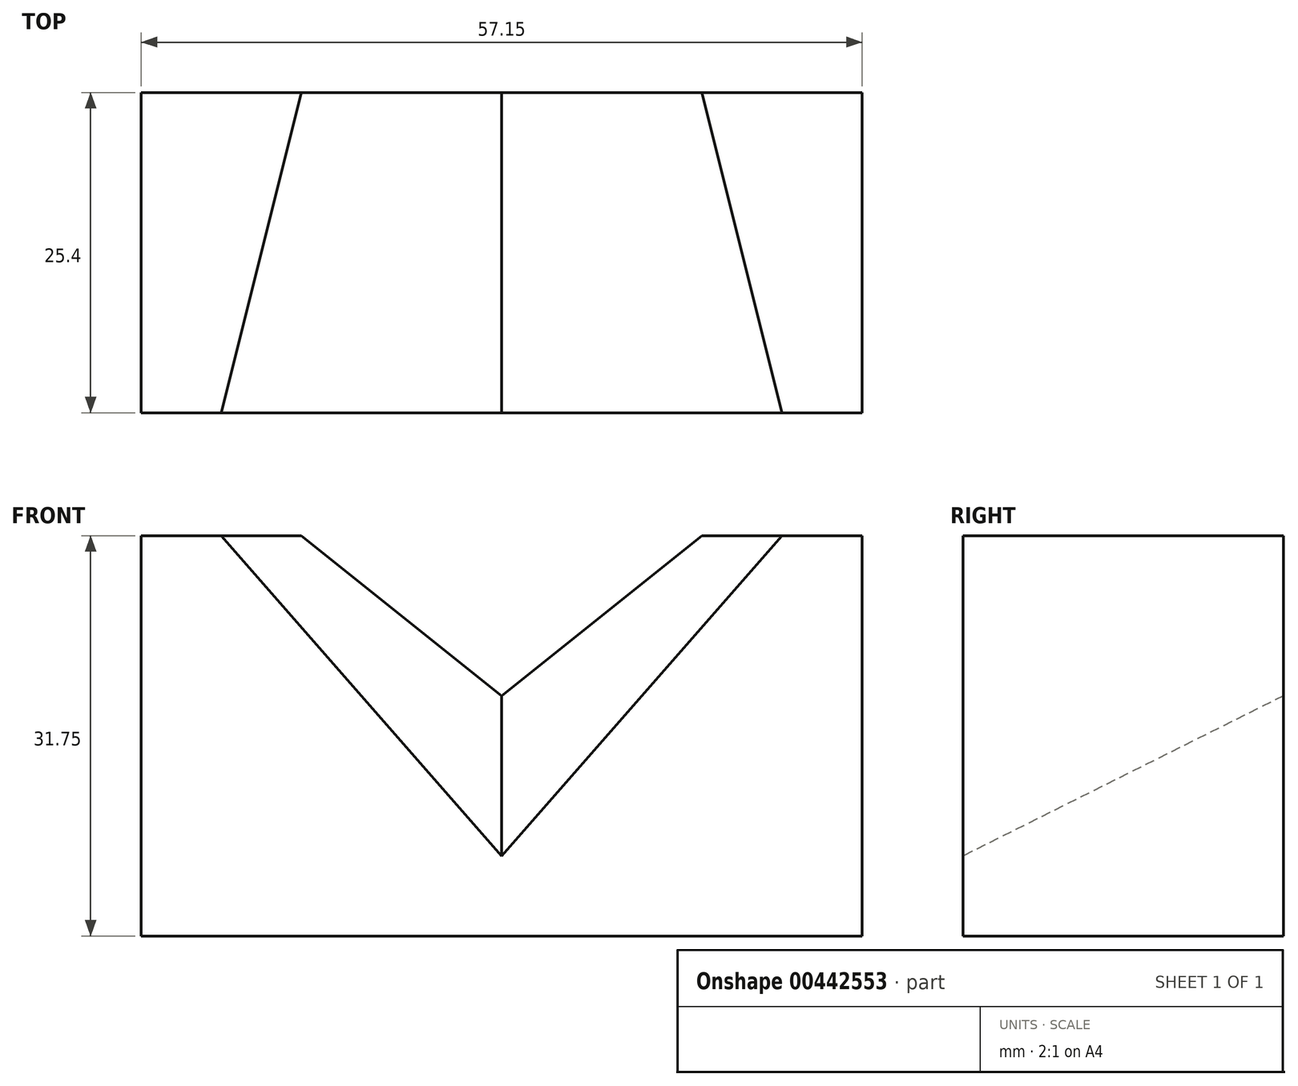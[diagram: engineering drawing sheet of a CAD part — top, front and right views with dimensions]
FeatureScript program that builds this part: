
annotation { "Feature Type Name" : "Feature", "Feature Type Description" : "" }
export const myFeature = defineFeature(function(context is Context, id is Id, definition is map)
    precondition{}
    {
        {
            var Q0;
            Q0=qCreatedBy(makeId("Front.planeOp"),FACE);
            var sketch = newSketch(context, id + "F0", { "sketchPlane" : qUnion([Q0])});
            skLineSegment(sketch, "E0.bottom", {"start": v(0, 0) * mm, "end": v(57.15, 0) * mm});
            skLineSegment(sketch, "E0.top", {"start": v(0, 31.75) * mm, "end": v(57.15, 31.75) * mm});
            skLineSegment(sketch, "E0.left", {"start": v(0, 0) * mm, "end": v(0, 31.75) * mm});
            skLineSegment(sketch, "E0.right", {"start": v(57.15, 0) * mm, "end": v(57.15, 31.75) * mm});
            skSolve(sketch);
        }
        {
            var Q0;
            Q0 = qSketchRegion(id + "F0", true);
            extrude(context, id + "F1", {"entities" : qUnion([Q0]), "depth" : 25.4 * mm});
        }
        {
            var Q0;
            Q0=makeQuery(id+"F1.opExtrude","CAP_FACE",FACE,{"disambiguationData":[OSD([sQuery(id+"F0.wireOp",EDGE,"E0.bottom"),sQuery(id+"F0.wireOp",EDGE,"E0.top"),sQuery(id+"F0.wireOp",EDGE,"E0.left"),sQuery(id+"F0.wireOp",EDGE,"E0.right")])],"isStart":false});
            var sketch = newSketch(context, id + "F2", { "sketchPlane" : qUnion([Q0])});
            skLineSegment(sketch, "E1", {"start": v(28.57, 0) * mm, "end": v(28.57, 6.35) * mm});
            skLineSegment(sketch, "E2", {"start": v(28.58, 6.35) * mm, "end": v(6.35, 31.75) * mm});
            skLineSegment(sketch, "E3", {"start": v(28.57, 6.35) * mm, "end": v(50.8, 31.75) * mm});
            skSolve(sketch);
        }
        {
            var Q0;
            Q0=makeQuery(id+"F1.opExtrude","CAP_FACE",FACE,{"disambiguationData":[OSD([sQuery(id+"F0.wireOp",EDGE,"E0.bottom"),sQuery(id+"F0.wireOp",EDGE,"E0.top"),sQuery(id+"F0.wireOp",EDGE,"E0.left"),sQuery(id+"F0.wireOp",EDGE,"E0.right")])],"isStart":true});
            var sketch = newSketch(context, id + "F3", { "sketchPlane" : qUnion([Q0])});
            skLineSegment(sketch, "E4", {"start": v(-28.57, 0) * mm, "end": v(-28.57, 19.05) * mm});
            skLineSegment(sketch, "E5", {"start": v(-28.57, 19.05) * mm, "end": v(-44.45, 31.75) * mm});
            skLineSegment(sketch, "E6", {"start": v(-28.58, 19.05) * mm, "end": v(-12.7, 31.75) * mm});
            skSolve(sketch);
        }
        {
            var Q1;
            {var subQ0=sQuery(id+"F3.wireOp",EDGE,"E5");Q1=makeQuery(id+"F3.imprint","IMPRINT",FACE,{"disambiguationData":[TD([[makeQuery(id+"F3.imprint","IMPRINT",EDGE,{"derivedFrom":subQ0}),-1.0]])]});}
            var Q2;
            {var subQ0=sQuery(id+"F2.wireOp",EDGE,"E2");Q2=makeQuery(id+"F2.imprint","IMPRINT",FACE,{"disambiguationData":[TD([[makeQuery(id+"F2.imprint","IMPRINT",EDGE,{"derivedFrom":subQ0}),-1.0]])]});}
            loft(context, id + "F4", {"operationType" : NewBodyOperationType.REMOVE, "sheetProfilesArray" : [{ "sheetProfileEntities" : qUnion([Q1]) }, { "sheetProfileEntities" : qUnion([Q2]) }]});
        }
    });
